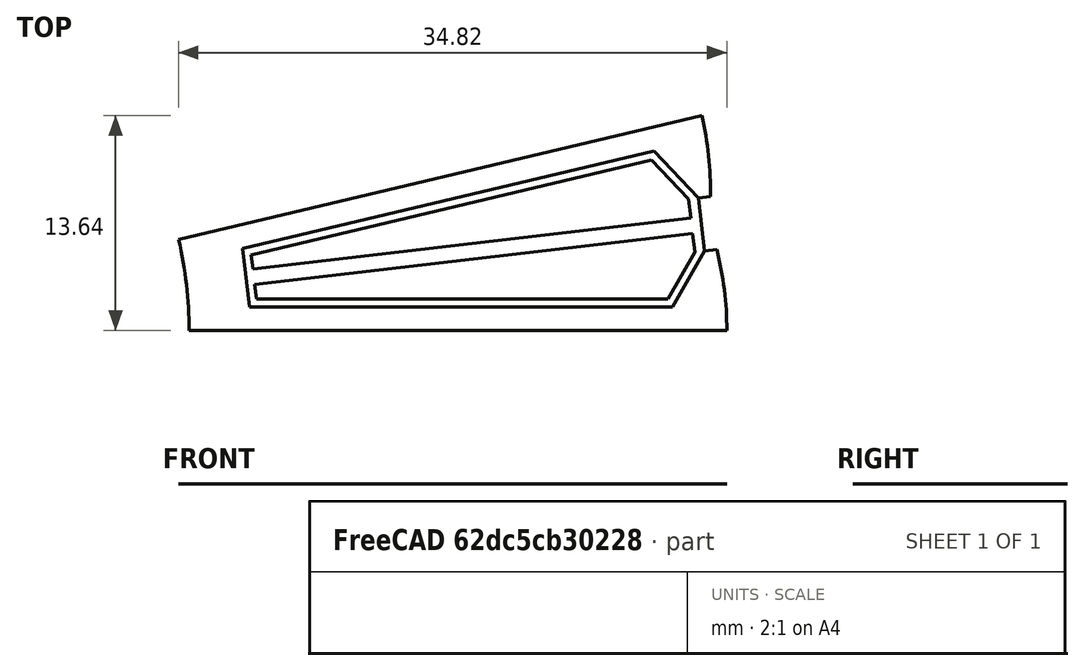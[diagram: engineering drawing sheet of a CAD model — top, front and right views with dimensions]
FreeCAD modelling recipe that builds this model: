
FCSTD DOCUMENT  (FreeCAD 0.18R4 (GitTag))
Label: StatorORNeedleWinding
License: All rights reserved
LicenseURL: http://en.wikipedia.org/wiki/All_rights_reserved
objects: Sketcher::SketchObject×8, Surface::Filling×4, PartDesign::Body×2, Spreadsheet::Sheet×1
note: 14 computed .brp shape members not serialized (recipe doc carries the construction recipe); baked Part::Feature solids carry a one-line shape summary decoded from their .brp

FEATURE [Spreadsheet::Sheet] Spreadsheet  label="Variables"
  cells = A2=slotNumber; B2(slotNumber)=27; A3=outerDiameter; B3(outerDiameter)=118.3; A4=innerDiameter; B4(innerDiameter)=50; A5=stackLength; B5(stackLength)=38; A6=stackingFactor; B6(stackingFactor)=0.95; A7=cuttingThickness; B7(cuttingThickness)=0.1; A8=skewAngle; B8(skewAngle)=0; A9=segmentAngle; B9(segmentAngle)==360 / slotNumber; A10=tipHeightReduction; B10(tipHeightReduction)=35; A11=toothThickness; B11(toothThickness)=3; A12=yokeThickness; B12(yokeThickness)=3.8; A13=tipHeight; B13(tipHeight)=1.2; A14=tipAngle; B14(tipAngle)=120; A15=openingLeft; B15(openingLeft)=1.7; A16=openingRight; B16(openingRight)=1.7; A17=slotIsolation; B17(slotIsolation)=0.5; A18=windingAngle; B18(windingAngle)=35; A19=heightRatio; B19(heightRatio)=45; A20=roundingRadii; B20(roundingRadii)=0.2; A21=phaseSeparation; B21(phaseSeparation)=1; A22=backWidth; B22(backWidth)=3; A23=axialOverhang; B23(axialOverhang)=1.2; A24=axialHeight; B24(axialHeight)=3
FEATURE [Sketcher::SketchObject] Sketch003  label="StatorSketch1"
  MapMode = 5
  Support = -> [XY_Plane]
  expr: Constraints[56] = Variables.innerDiameter / 2 + Variables.yokeThickness
  expr: Constraints[52] = Variables.innerDiameter / 2
  expr: Constraints[44] = Variables.toothThickness / 2
  expr: Constraints[40] = Variables.tipAngle
  expr: Constraints[38] = Variables.tipAngle
  expr: Constraints[27] = Variables.tipHeight * (1 - Variables.tipHeightReduction / 100)
  expr: Constraints[14] = Variables.openingLeft
  expr: Constraints[21] = Variables.tipHeight
  expr: Constraints[18] = Variables.openingRight
  expr: Constraints[10] = Variables.segmentAngle / 2
  expr: Constraints[7] = Variables.outerDiameter / 2
  expr: Constraints[6] = Variables.segmentAngle
  sketch-geometry (23):
    g0: LineSegment [constr] StartX=0 StartY=0 StartZ=0 EndX=59.15 EndY=0 EndZ=0
    g1: LineSegment [constr] StartX=0 StartY=0 StartZ=0 EndX=57.5556 EndY=13.6409 EndZ=0
    g2: ArcOfCircle [constr] CenterX=0 CenterY=0 CenterZ=0 NormalX=0 NormalY=0 NormalZ=1 AngleXU=0 Radius=59.15 StartAngle=0 EndAngle=0.232711
    g3: LineSegment [constr] StartX=0 StartY=0 StartZ=0 EndX=58.75 EndY=6.8669 EndZ=0
    g4: LineSegment [constr] StartX=58.5284 StartY=8.55256 StartZ=0 EndX=58.7258 EndY=6.86406 EndZ=0
    g5: LineSegment [constr] StartX=58.7258 StartY=6.86406 StartZ=0 EndX=58.9231 EndY=5.17555 EndZ=0
    g6: LineSegment [constr] StartX=58.5284 StartY=8.55256 StartZ=0 EndX=57.3365 EndY=8.41325 EndZ=0
    g7: LineSegment [constr] StartX=58.9231 StartY=5.17555 StartZ=0 EndX=57.7313 EndY=5.03624 EndZ=0
    g8: LineSegment StartX=57.3365 StartY=8.41325 StartZ=0 EndX=58.1113 EndY=8.50381 EndZ=0
    g9: LineSegment StartX=57.3365 StartY=8.41325 StartZ=0 EndX=54.5344 EndY=11.3833 EndZ=0
    g10: LineSegment StartX=54.5344 StartY=11.3833 StartZ=0 EndX=28.3898 EndY=5.18695 EndZ=0
    g11: LineSegment StartX=28.3898 StartY=5.18695 StartZ=0 EndX=28.8207 EndY=1.5 EndZ=0
    g12: LineSegment StartX=28.8207 StartY=1.5 StartZ=0 EndX=55.6896 EndY=1.5 EndZ=0
    g13: LineSegment StartX=55.6896 StartY=1.5 StartZ=0 EndX=57.7313 EndY=5.03624 EndZ=0
    g14: LineSegment StartX=57.7313 StartY=5.03624 StartZ=0 EndX=58.506 EndY=5.12679 EndZ=0
    g15: LineSegment [constr] StartX=28.8207 StartY=1.5 StartZ=0 EndX=28.8207 EndY=0 EndZ=0
    g16: LineSegment [constr] StartX=28.3898 StartY=5.18695 StartZ=0 EndX=28.0439 EndY=6.64652 EndZ=0
    g17: ArcOfCircle CenterX=0 CenterY=0 CenterZ=0 NormalX=0 NormalY=0 NormalZ=1 AngleXU=0 Radius=25 StartAngle=0 EndAngle=0.232711
    g18: ArcOfCircle [constr] CenterX=0 CenterY=0 CenterZ=0 NormalX=0 NormalY=0 NormalZ=1 AngleXU=0 Radius=28.8 StartAngle=0 EndAngle=0.232711
    g19: ArcOfCircle CenterX=37.3862 CenterY=8.86069 CenterZ=0 NormalX=0 NormalY=0 NormalZ=1 AngleXU=0 Radius=20.7281 StartAngle=6.26597 EndAngle=6.5159
    g20: ArcOfCircle CenterX=38.4219 CenterY=0 CenterZ=0 NormalX=0 NormalY=0 NormalZ=1 AngleXU=0 Radius=20.7281 StartAngle=0 EndAngle=0.249929
    g21: LineSegment StartX=57.5556 StartY=13.6409 StartZ=0 EndX=24.3261 EndY=5.7654 EndZ=0
    g22: LineSegment StartX=25 StartY=0 StartZ=0 EndX=59.15 EndY=0 EndZ=0
  constraints (69):
    c: Coincident(g0,g-1)
    c: PointOnObject(g0,g-1)
    c: Coincident(g1,g-1)
    c: Coincident(g2,g-1)
    c: Coincident(g2,g0)
    c: Coincident(g2,g1)
    c: Angle(g0,g1) = 0.232711
    c: Radius(g2) = 59.15
    c: Coincident(g3,g-1)
    c: PointOnObject(g3,g2)
    c: Angle(g0,g3) = 0.116355
    c: PointOnObject(g4,g2)
    c: PointOnObject(g4,g3)
    c: Angle(g4,g3) = 1.5708
    c: Distance(g4) = 1.7
    c: PointOnObject(g5,g3)
    c: PointOnObject(g5,g2)
    c: Angle(g3,g5) = 1.5708
    c: Distance(g5) = 1.7
    c: Coincident(g6,g4)
    c: Angle(g6,g4) = 1.5708
    c: Distance(g6) = 1.2
    c: Coincident(g7,g5)
    c: Angle(g5,g7) = 1.5708
    c: Equal(g7,g6)
    c: Coincident(g8,g6)
    c: PointOnObject(g8,g6)
    c: Distance(g8) = 0.78
    c: Coincident(g9,g8)
    c: Coincident(g10,g9)
    c: Coincident(g11,g10)
    c: Coincident(g12,g11)
    c: Coincident(g13,g12)
    c: Coincident(g13,g7)
    c: Coincident(g14,g13)
    c: PointOnObject(g14,g7)
    c: Equal(g14,g8)
    c: Horizontal(g12)
    c: Angle(g13,g12) = 2.0944
    c: Parallel(g1,g10)
    c: Angle(g10,g9) = 2.0944
    c: Coincident(g15,g11)
    c: PointOnObject(g15,g0)
    c: Vertical(g15)
    c: DistanceY(g15,g15) = 1.5
    c: Coincident(g16,g10)
    c: PointOnObject(g16,g1)
    c: Angle(g1,g16) = 1.5708
    c: Equal(g16,g15)
    c: Coincident(g17,g-1)
    c: PointOnObject(g17,g1)
    c: PointOnObject(g17,g0)
    c: Radius(g17) = 25
    c: Coincident(g18,g-1)
    c: PointOnObject(g18,g1)
    c: PointOnObject(g18,g0)
    c: Radius(g18) = 28.8
    c: Angle(g3,g11) = 1.5708
    c: Tangent(g18,g11)
    c: PointOnObject(g19,g1)
    c: Coincident(g19,g1)
    c: Coincident(g19,g8)
    c: PointOnObject(g20,g0)
    c: Coincident(g20,g14)
    c: Coincident(g20,g0)
    c: Coincident(g21,g19)
    c: Coincident(g21,g17)
    c: Coincident(g22,g17)
    c: Coincident(g22,g20)
FEATURE [Sketcher::SketchObject] Sketch  label="StatorStack"
  MapMode = 5
  Support = -> [XY_Plane001]
  expr: Constraints[18] = Variables.innerDiameter / 2
  expr: Constraints[10] = Variables.outerDiameter / 2
  expr: Constraints[9] = Variables.innerDiameter / 2
  expr: Constraints[8] = Variables.stackLength
  sketch-geometry (8):
    g0: LineSegment StartX=-19 StartY=25 StartZ=0 EndX=19 EndY=25 EndZ=0
    g1: LineSegment StartX=19 StartY=25 StartZ=0 EndX=19 EndY=59.15 EndZ=0
    g2: LineSegment StartX=19 StartY=59.15 StartZ=0 EndX=-19 EndY=59.15 EndZ=0
    g3: LineSegment StartX=-19 StartY=59.15 StartZ=0 EndX=-19 EndY=25 EndZ=0
    g4: LineSegment StartX=-19 StartY=-25 StartZ=0 EndX=19 EndY=-25 EndZ=0
    g5: LineSegment StartX=19 StartY=-25 StartZ=0 EndX=19 EndY=-59.15 EndZ=0
    g6: LineSegment StartX=19 StartY=-59.15 StartZ=0 EndX=-19 EndY=-59.15 EndZ=0
    g7: LineSegment StartX=-19 StartY=-59.15 StartZ=0 EndX=-19 EndY=-25 EndZ=0
  constraints (22):
    c: Coincident(g0,g1)
    c: Coincident(g1,g2)
    c: Coincident(g2,g3)
    c: Coincident(g3,g0)
    c: Horizontal(g2)
    c: Vertical(g1)
    c: Vertical(g3)
    c: Symmetric(g0,g0,g-2)
    c: DistanceX(g0,g0) = 38
    c: DistanceY(g-1,g0) = 25
    c: DistanceY(g-1,g1) = 59.15
    c: Coincident(g4,g5)
    c: Coincident(g5,g6)
    c: Coincident(g6,g7)
    c: Coincident(g7,g4)
    c: Horizontal(g6)
    c: Equal(g4,g0)
    c: Symmetric(g4,g4,g-2)
    c: DistanceY(g4,g-1) = 25
    c: Equal(g7,g3)
    c: Angle(g7,g4) = 1.5708
    c: Angle(g4,g5) = 1.5708
FEATURE [Sketcher::SketchObject] Sketch004  label="SlotSketch"
  ExternalGeometry = -> [Sketch003]
  MapMode = 5
  Support = -> [XY_Plane]
  sketch-geometry (6):
    g0: LineSegment StartX=57.3365 StartY=8.41325 StartZ=0 EndX=54.5344 EndY=11.3833 EndZ=0
    g1: LineSegment StartX=54.5344 StartY=11.3833 StartZ=0 EndX=28.3898 EndY=5.18695 EndZ=0
    g2: LineSegment StartX=28.3898 StartY=5.18695 StartZ=0 EndX=28.8207 EndY=1.5 EndZ=0
    g3: LineSegment StartX=28.8207 StartY=1.5 StartZ=0 EndX=55.6896 EndY=1.5 EndZ=0
    g4: LineSegment StartX=55.6896 StartY=1.5 StartZ=0 EndX=57.7313 EndY=5.03624 EndZ=0
    g5: LineSegment StartX=57.7313 StartY=5.03624 StartZ=0 EndX=57.3365 EndY=8.41325 EndZ=0
  constraints (12):
    c: Coincident(g0,g-3)
    c: Coincident(g0,g-4)
    c: Coincident(g1,g0)
    c: Coincident(g1,g-5)
    c: Coincident(g2,g1)
    c: Coincident(g2,g-6)
    c: Coincident(g3,g-7)
    c: Coincident(g3,g2)
    c: Coincident(g4,g3)
    c: Coincident(g4,g-7)
    c: Coincident(g5,g4)
    c: Coincident(g5,g0)
FEATURE [Sketcher::SketchObject] Sketch005  label="TerminalLeftSketch"
  ExternalGeometry = -> [Sketch003]
  MapMode = 5
  Support = -> [XY_Plane]
  expr: Constraints[32] = Variables.slotIsolation
  expr: Constraints[22] = Variables.phaseSeparation / 2
  expr: Constraints[18] = Variables.segmentAngle / 2
  sketch-geometry (12):
    g0: LineSegment StartX=56.7174 StartY=8.34089 StartZ=0 EndX=54.3688 EndY=10.8302 EndZ=0
    g1: LineSegment StartX=54.3688 StartY=10.8302 StartZ=0 EndX=28.9381 EndY=4.80304 EndZ=0
    g2: LineSegment StartX=28.9381 StartY=4.80304 StartZ=0 EndX=29.0438 EndY=3.89814 EndZ=0
    g3: LineSegment StartX=29.0438 StartY=3.89814 StartZ=0 EndX=56.8567 EndY=7.149 EndZ=0
    g4: LineSegment StartX=56.8567 StartY=7.149 StartZ=0 EndX=56.7174 EndY=8.34089 EndZ=0
    g5: LineSegment [constr] StartX=54.3688 StartY=10.8302 StartZ=0 EndX=54.7325 EndY=11.1734 EndZ=0
    g6: LineSegment [constr] StartX=54.3688 StartY=10.8302 StartZ=0 EndX=54.2535 EndY=11.3168 EndZ=0
    g7: LineSegment [constr] StartX=28.9381 StartY=4.80304 StartZ=0 EndX=28.4415 EndY=4.745 EndZ=0
    g8: LineSegment [constr] StartX=56.7174 StartY=8.34089 StartZ=0 EndX=57.3365 EndY=8.41325 EndZ=0
    g9: LineSegment [constr] StartX=57.3365 StartY=8.41325 StartZ=0 EndX=57.7313 EndY=5.03624 EndZ=0
    g10: LineSegment [constr] StartX=0 StartY=0 StartZ=0 EndX=57.5339 EndY=6.72475 EndZ=0
    g11: LineSegment [constr] StartX=56.8567 StartY=7.149 StartZ=0 EndX=56.9148 EndY=6.65238 EndZ=0
  constraints (34):
    c: Coincident(g1,g0)
    c: Coincident(g2,g1)
    c: Coincident(g3,g2)
    c: Coincident(g4,g3)
    c: Coincident(g4,g0)
    c: Angle(g3,g2) = 1.5708
    c: Coincident(g5,g0)
    c: Coincident(g6,g0)
    c: Angle(g0,g5) = 1.5708
    c: Equal(g6,g5)
    c: Coincident(g7,g1)
    c: Angle(g7,g2) = 1.5708
    c: Equal(g7,g6)
    c: Coincident(g8,g0)
    c: Parallel(g4,g2)
    c: Coincident(g9,g8)
    c: Coincident(g10,g-1)
    c: PointOnObject(g10,g9)
    c: Angle(g-1,g10) = 0.116355
    c: Coincident(g11,g3)
    c: PointOnObject(g11,g10)
    c: Angle(g11,g10) = 1.5708
    c: Distance(g11) = 0.5
    c: Angle(g8,g9) = 1.5708
    c: PointOnObject(g5,g-3)
    c: Coincident(g8,g-3)
    c: Coincident(g9,g-6)
    c: PointOnObject(g6,g-4)
    c: Parallel(g0,g-3)
    c: Parallel(g1,g-4)
    c: PointOnObject(g7,g-5)
    c: Parallel(g2,g-5)
    c: Distance(g5) = 0.5
    c: Angle(g-4,g6) = 1.5708
FEATURE [Sketcher::SketchObject] Sketch006  label="TerminalRightSketch"
  ExternalGeometry = -> [Sketch003]
  MapMode = 5
  Support = -> [XY_Plane]
  expr: Constraints[24] = Variables.phaseSeparation / 2
  expr: Constraints[2] = Variables.segmentAngle / 2
  expr: Constraints[17] = Variables.slotIsolation
  sketch-geometry (12):
    g0: LineSegment [constr] StartX=57.3365 StartY=8.41325 StartZ=0 EndX=57.7313 EndY=5.03624 EndZ=0
    g1: LineSegment [constr] StartX=0 StartY=0 StartZ=0 EndX=57.5339 EndY=6.72475 EndZ=0
    g2: LineSegment StartX=57.1121 StartY=4.96388 StartZ=0 EndX=55.4009 EndY=2 EndZ=0
    g3: LineSegment StartX=55.4009 StartY=2 StartZ=0 EndX=29.2657 EndY=2 EndZ=0
    g4: LineSegment StartX=29.2657 StartY=2 StartZ=0 EndX=29.1599 EndY=2.9049 EndZ=0
    g5: LineSegment StartX=29.1599 StartY=2.9049 StartZ=0 EndX=56.9728 EndY=6.15576 EndZ=0
    g6: LineSegment StartX=56.9728 StartY=6.15576 StartZ=0 EndX=57.1121 EndY=4.96388 EndZ=0
    g7: LineSegment [constr] StartX=57.1121 StartY=4.96388 StartZ=0 EndX=57.7313 EndY=5.03624 EndZ=0
    g8: LineSegment [constr] StartX=55.4009 StartY=2 StartZ=0 EndX=55.8339 EndY=1.75 EndZ=0
    g9: LineSegment [constr] StartX=55.4009 StartY=2 StartZ=0 EndX=55.4009 EndY=1.5 EndZ=0
    g10: LineSegment [constr] StartX=29.1599 StartY=2.9049 StartZ=0 EndX=28.6633 EndY=2.84686 EndZ=0
    g11: LineSegment [constr] StartX=56.9728 StartY=6.15576 StartZ=0 EndX=56.9148 EndY=6.65238 EndZ=0
  constraints (34):
    c: Coincident(g1,g-1)
    c: PointOnObject(g1,g0)
    c: Angle(g-1,g1) = 0.116355
    c: Coincident(g3,g2)
    c: Horizontal(g3)
    c: Coincident(g4,g3)
    c: Coincident(g5,g4)
    c: Coincident(g6,g5)
    c: Coincident(g6,g2)
    c: Parallel(g5,g1)
    c: Coincident(g7,g2)
    c: Coincident(g7,g0)
    c: Angle(g0,g7) = 1.5708
    c: Coincident(g8,g2)
    c: Coincident(g9,g2)
    c: Equal(g9,g8)
    c: Angle(g3,g9) = 1.5708
    c: Distance(g9) = 0.5
    c: Coincident(g10,g4)
    c: Angle(g10,g4) = 1.5708
    c: Equal(g10,g9)
    c: Coincident(g11,g5)
    c: PointOnObject(g11,g1)
    c: Angle(g1,g11) = 1.5708
    c: Distance(g11) = 0.5
    c: Parallel(g6,g0)
    c: PointOnObject(g10,g-6)
    c: Parallel(g4,g-6)
    c: PointOnObject(g9,g-5)
    c: PointOnObject(g8,g-4)
    c: Angle(g-4,g8) = 1.5708
    c: Coincident(g0,g-4)
    c: Coincident(g0,g-3)
    c: Parallel(g2,g-4)
FEATURE [Sketcher::SketchObject] Sketch007  label="YokeLine"
  ExternalGeometry = -> [Sketch003]
  MapMode = 5
  Support = -> [XY_Plane]
  expr: Constraints[7] = Variables.segmentAngle / 2
  expr: Constraints[0] = Variables.yokeThickness
  sketch-geometry (3):
    g0: LineSegment StartX=28.6053 StartY=3.34348 StartZ=0 EndX=24.831 EndY=2.90232 EndZ=0
    g1: LineSegment [constr] StartX=24.3261 StartY=5.7654 StartZ=0 EndX=25 EndY=0 EndZ=0
    g2: LineSegment [constr] StartX=0 StartY=0 StartZ=0 EndX=24.831 EndY=2.90232 EndZ=0
  constraints (8):
    c: Distance(g0) = 3.8
    c: PointOnObject(g0,g-3)
    c: Coincident(g1,g-3)
    c: Coincident(g1,g-3)
    c: Angle(g0,g1) = 1.5708
    c: Coincident(g2,g-1)
    c: Coincident(g2,g0)
    c: Angle(g-1,g2) = 0.116355
FEATURE [Sketcher::SketchObject] Sketch008  label="ToothLine"
  ExternalGeometry = -> [Sketch003]
  MapMode = 5
  Support = -> [XY_Plane]
  expr: Constraints[2] = Variables.toothThickness
  sketch-geometry (3):
    g0: LineSegment StartX=41.4621 StartY=8.28515 StartZ=0 EndX=40.7703 EndY=11.2043 EndZ=0
    g1: LineSegment [constr] StartX=28.3898 StartY=5.18695 StartZ=0 EndX=41.4621 EndY=8.28515 EndZ=0
    g2: LineSegment [constr] StartX=41.4621 StartY=8.28515 StartZ=0 EndX=54.5344 EndY=11.3833 EndZ=0
  constraints (8):
    c: PointOnObject(g0,g-3)
    c: Angle(g0,g-3) = 1.5708
    c: Distance(g0) = 3
    c: Coincident(g1,g-3)
    c: Coincident(g1,g0)
    c: Coincident(g2,g0)
    c: Coincident(g2,g-3)
    c: Equal(g1,g2)
FEATURE [PartDesign::Body] Body  label="TopView"
  Group = -> [Sketch003,Sketch004,Sketch005,Sketch006,Sketch007,Sketch008]
  Origin = -> Origin
FEATURE [Surface::Filling] Surface001  label="TerminalLeftSketch_Surface"
  Anisotropy = false
  BoundaryEdges = -> [Sketch005]
  BoundaryOrder = [0,0,0,0,0]
  Degree = 3
  Iterations = 2
  MaximumDegree = 8
  MaximumSegments = 9
  PointsOnCurve = 15
  TolAngular = 0.01
  TolCurvature = 0.1
  Tolerance2d = 1e-05
  Tolerance3d = 0.0001
FEATURE [Surface::Filling] Surface002  label="TerminalRightSketch_Surface"
  Anisotropy = false
  BoundaryEdges = -> [Sketch006]
  BoundaryOrder = [0,0,0,0,0]
  Degree = 3
  Iterations = 2
  MaximumDegree = 8
  MaximumSegments = 9
  PointsOnCurve = 15
  TolAngular = 0.01
  TolCurvature = 0.1
  Tolerance2d = 1e-05
  Tolerance3d = 0.0001
FEATURE [Surface::Filling] Surface003  label="StatorSketch1_Surface"
  Anisotropy = false
  BoundaryEdges = -> [Sketch003]
  BoundaryOrder = [0,0,0,0,0,0,0,0,0,0,0,0]
  Degree = 3
  Iterations = 2
  MaximumDegree = 8
  MaximumSegments = 9
  PointsOnCurve = 15
  TolAngular = 0.01
  TolCurvature = 0.1
  Tolerance2d = 1e-05
  Tolerance3d = 0.0001
FEATURE [Surface::Filling] Surface  label="SlotSketch_Surface"
  Anisotropy = false
  BoundaryEdges = -> [Sketch004]
  BoundaryOrder = [0,0,0,0,0,0]
  Degree = 3
  Iterations = 2
  MaximumDegree = 8
  MaximumSegments = 9
  PointsOnCurve = 15
  TolAngular = 0.01
  TolCurvature = 0.1
  Tolerance2d = 1e-05
  Tolerance3d = 0.0001
FEATURE [Sketcher::SketchObject] Sketch012  label="Isolation"
  ExternalGeometry = -> [Sketch]
  MapMode = 5
  Support = -> [XY_Plane001]
  expr: Constraints[79] = Variables.axialHeight
  expr: Constraints[15] = Variables.axialHeight / 2
  expr: Constraints[18] = (Variables.outerDiameter - Variables.innerDiameter) / 2 - Variables.yokeThickness - Variables.tipHeight
  expr: Constraints[17] = Variables.tipHeight
  expr: Constraints[14] = Variables.axialHeight + Variables.axialOverhang
  expr: Constraints[16] = Variables.yokeThickness
  sketch-geometry (32):
    g0: LineSegment StartX=-19 StartY=59.15 StartZ=0 EndX=-19 EndY=25 EndZ=0
    g1: LineSegment StartX=-19 StartY=25 StartZ=0 EndX=-24.7 EndY=25 EndZ=0
    g2: LineSegment StartX=-24.7 StartY=25 StartZ=0 EndX=-24.7 EndY=28.8 EndZ=0
    g3: LineSegment StartX=-24.7 StartY=28.8 StartZ=0 EndX=-21.7 EndY=28.8 EndZ=0
    g4: LineSegment StartX=-21.7 StartY=28.8 StartZ=0 EndX=-21.7 EndY=57.95 EndZ=0
    g5: LineSegment StartX=-21.7 StartY=57.95 StartZ=0 EndX=-23.2 EndY=57.95 EndZ=0
    g6: LineSegment StartX=-23.2 StartY=57.95 StartZ=0 EndX=-23.2 EndY=59.15 EndZ=0
    g7: LineSegment StartX=-23.2 StartY=59.15 StartZ=0 EndX=-19 EndY=59.15 EndZ=0
    g8: LineSegment StartX=-24.7 StartY=-25 StartZ=0 EndX=-19 EndY=-25 EndZ=0
    g9: LineSegment StartX=-19 StartY=-25 StartZ=0 EndX=-19 EndY=-59.15 EndZ=0
    g10: LineSegment StartX=-19 StartY=-59.15 StartZ=0 EndX=-23.2 EndY=-59.15 EndZ=0
    g11: LineSegment StartX=-23.2 StartY=-59.15 StartZ=0 EndX=-23.2 EndY=-57.95 EndZ=0
    g12: LineSegment StartX=-23.2 StartY=-57.95 StartZ=0 EndX=-21.7 EndY=-57.95 EndZ=0
    g13: LineSegment StartX=-21.7 StartY=-57.95 StartZ=0 EndX=-21.7 EndY=-28.8 EndZ=0
    g14: LineSegment StartX=-21.7 StartY=-28.8 StartZ=0 EndX=-24.7 EndY=-28.8 EndZ=0
    g15: LineSegment StartX=-24.7 StartY=-28.8 StartZ=0 EndX=-24.7 EndY=-25 EndZ=0
    g16: LineSegment StartX=23.2 StartY=59.15 StartZ=0 EndX=19 EndY=59.15 EndZ=0
    g17: LineSegment StartX=19 StartY=59.15 StartZ=0 EndX=19 EndY=25 EndZ=0
    g18: LineSegment StartX=19 StartY=25 StartZ=0 EndX=24.7 EndY=25 EndZ=0
    g19: LineSegment StartX=24.7 StartY=25 StartZ=0 EndX=24.7 EndY=28.8 EndZ=0
    g20: LineSegment StartX=24.7 StartY=28.8 StartZ=0 EndX=21.7 EndY=28.8 EndZ=0
    g21: LineSegment StartX=21.7 StartY=28.8 StartZ=0 EndX=21.7 EndY=57.95 EndZ=0
    g22: LineSegment StartX=21.7 StartY=57.95 StartZ=0 EndX=23.2 EndY=57.95 EndZ=0
    g23: LineSegment StartX=23.2 StartY=57.95 StartZ=0 EndX=23.2 EndY=59.15 EndZ=0
    g24: LineSegment StartX=24.7 StartY=-25 StartZ=0 EndX=19 EndY=-25 EndZ=0
    g25: LineSegment StartX=19 StartY=-25 StartZ=0 EndX=19 EndY=-59.15 EndZ=0
    g26: LineSegment StartX=19 StartY=-59.15 StartZ=0 EndX=23.2 EndY=-59.15 EndZ=0
    g27: LineSegment StartX=23.2 StartY=-59.15 StartZ=0 EndX=23.2 EndY=-57.95 EndZ=0
    g28: LineSegment StartX=23.2 StartY=-57.95 StartZ=0 EndX=21.7 EndY=-57.95 EndZ=0
    g29: LineSegment StartX=21.7 StartY=-57.95 StartZ=0 EndX=21.7 EndY=-28.8 EndZ=0
    g30: LineSegment StartX=21.7 StartY=-28.8 StartZ=0 EndX=24.7 EndY=-28.8 EndZ=0
    g31: LineSegment StartX=24.7 StartY=-28.8 StartZ=0 EndX=24.7 EndY=-25 EndZ=0
  constraints (92):
    c: Vertical(g0)
    c: Coincident(g1,g0)
    c: Horizontal(g1)
    c: Coincident(g2,g1)
    c: Coincident(g3,g2)
    c: Horizontal(g3)
    c: Coincident(g4,g3)
    c: Vertical(g4)
    c: Coincident(g5,g4)
    c: Horizontal(g5)
    c: Coincident(g7,g6)
    c: Coincident(g7,g0)
    c: Horizontal(g7)
    c: Coincident(g6,g5)
    c: DistanceX(g7,g7) = 4.2
    c: DistanceX(g5,g5) = 1.5
    c: DistanceY(g2,g2) = 3.8
    c: DistanceY(g6,g6) = 1.2
    c: DistanceY(g4,g4) = 29.15
    c: Coincident(g0,g-6)
    c: Coincident(g8,g9)
    c: Vertical(g9)
    c: Coincident(g9,g10)
    c: Coincident(g10,g11)
    c: Coincident(g11,g12)
    c: Coincident(g12,g13)
    c: Vertical(g13)
    c: Coincident(g13,g14)
    c: Coincident(g14,g15)
    c: Coincident(g15,g8)
    c: Equal(g7,g10)
    c: Equal(g13,g4)
    c: Equal(g9,g0)
    c: Equal(g11,g6)
    c: Coincident(g8,g-4)
    c: Coincident(g16,g17)
    c: Vertical(g17)
    c: Coincident(g17,g18)
    c: Coincident(g18,g19)
    c: Coincident(g19,g20)
    c: Coincident(g20,g21)
    c: Vertical(g21)
    c: Coincident(g21,g22)
    c: Coincident(g22,g23)
    c: Coincident(g23,g16)
    c: Vertical(g23)
    c: Equal(g0,g17)
    c: Equal(g16,g7)
    c: Equal(g2,g19)
    c: Equal(g6,g23)
    c: Coincident(g-3,g16)
    c: Coincident(g24,g25)
    c: Vertical(g25)
    c: Coincident(g25,g26)
    c: Coincident(g26,g27)
    c: Coincident(g27,g28)
    c: Coincident(g28,g29)
    c: Vertical(g29)
    c: Coincident(g29,g30)
    c: Coincident(g30,g31)
    c: Coincident(g31,g24)
    c: Equal(g8,g24)
    c: Equal(g10,g26)
    c: Equal(g11,g27)
    c: Equal(g15,g31)
    c: Equal(g9,g25)
    c: Coincident(g24,g-5)
    c: Angle(g17,g16) = 1.5708
    c: Angle(g21,g22) = 1.5708
    c: Angle(g18,g17) = 1.5708
    c: Angle(g20,g21) = 1.5708
    c: Angle(g25,g24) = 1.5708
    c: Angle(g29,g30) = 1.5708
    c: Angle(g28,g29) = 1.5708
    c: Angle(g26,g25) = 1.5708
    c: Angle(g14,g13) = 1.5708
    c: Angle(g13,g12) = 1.5708
    c: Angle(g9,g10) = 1.5708
    c: Angle(g8,g9) = 1.5708
    c: DistanceX(g3,g3) = 3
    c: Angle(g6,g7) = 1.5708
    c: Equal(g20,g3)
    c: Equal(g3,g14)
    c: Angle(g15,g8) = 1.5708
    c: Equal(g12,g5)
    c: Equal(g28,g5)
    c: Equal(g5,g22)
    c: Angle(g24,g31) = 1.5708
    c: Angle(g19,g18) = 1.5708
    c: Angle(g1,g2) = 1.5708
    c: Angle(g10,g11) = 1.5708
    c: Angle(g27,g26) = 1.5708
FEATURE [PartDesign::Body] Body001  label="SideView"
  Group = -> [Sketch,Sketch012]
  Origin = -> Origin001
